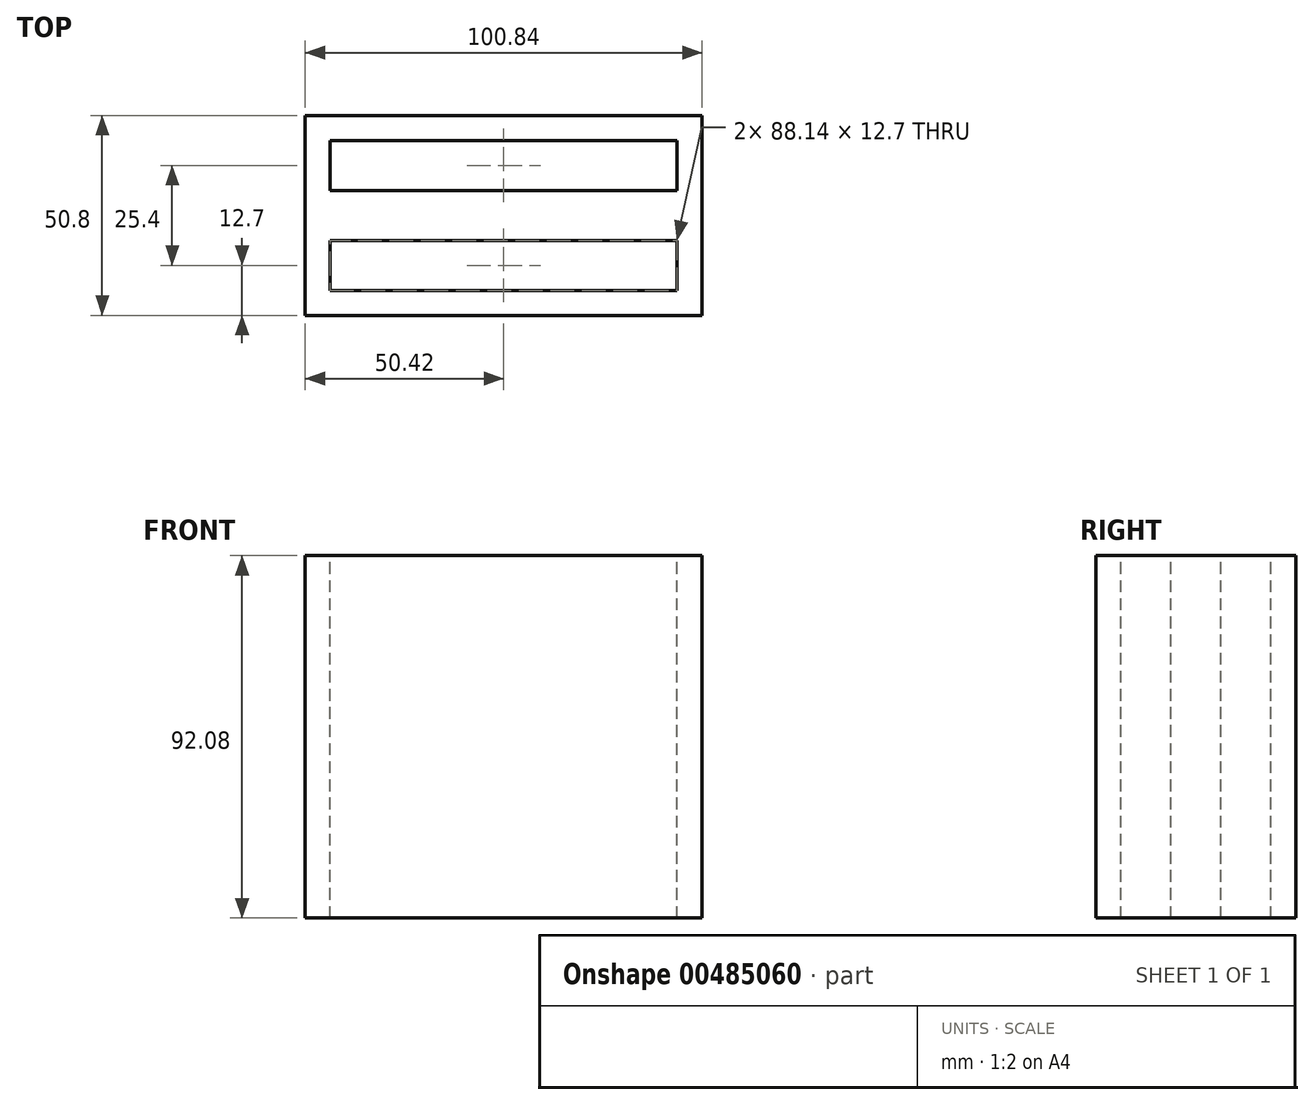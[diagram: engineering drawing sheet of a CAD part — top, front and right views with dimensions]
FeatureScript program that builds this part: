
annotation { "Feature Type Name" : "Feature", "Feature Type Description" : "" }
export const myFeature = defineFeature(function(context is Context, id is Id, definition is map)
    precondition{}
    {
        {
            var Q0;
            Q0=qCreatedBy(makeId("Front.planeOp"),FACE);
            var sketch = newSketch(context, id + "F0", { "sketchPlane" : qUnion([Q0])});
            skLineSegment(sketch, "E0.bottom", {"start": v(50.42, 46.04) * mm, "end": v(-50.42, 46.04) * mm});
            skLineSegment(sketch, "E0.top", {"start": v(50.42, -46.04) * mm, "end": v(-50.42, -46.04) * mm});
            skLineSegment(sketch, "E0.left", {"start": v(50.42, 46.04) * mm, "end": v(50.42, -46.04) * mm});
            skLineSegment(sketch, "E0.right", {"start": v(-50.42, 46.04) * mm, "end": v(-50.42, -46.04) * mm});
            skPoint(sketch, "E0.middle", {"position": v(0, 0) * mm});
            skSolve(sketch);
        }
        {
            var Q0;
            Q0 = qSketchRegion(id + "F0", true);
            extrude(context, id + "F1", {"entities" : qUnion([Q0]), "depth" : 50.8 * mm});
        }
        {
            var Q0;
            Q0=makeQuery(id+"F1.opExtrude","SWEPT_FACE",FACE,{"disambiguationData":[OSD([sQuery(id+"F0.wireOp",EDGE,"E0.bottom")])]});
            var sketch = newSketch(context, id + "F2", { "sketchPlane" : qUnion([Q0])});
            skLineSegment(sketch, "E1", {"start": v(50.42, 0) * mm, "end": v(-50.42, 0) * mm});
            skLineSegment(sketch, "E2.0", {"start": v(-44.07, -31.75) * mm, "end": v(44.07, -31.75) * mm});
            skLineSegment(sketch, "E2.1", {"start": v(-44.07, -31.75) * mm, "end": v(-44.07, -44.45) * mm});
            skLineSegment(sketch, "E2.2", {"start": v(-44.07, -44.45) * mm, "end": v(44.07, -44.45) * mm});
            skLineSegment(sketch, "E2.3", {"start": v(44.07, -44.45) * mm, "end": v(44.07, -31.75) * mm});
            skLineSegment(sketch, "E3.MirrorCS", {"start": v(-44.07, -19.05) * mm, "end": v(44.07, -19.05) * mm});
            skLineSegment(sketch, "E4.MirrorCS", {"start": v(44.07, -6.35) * mm, "end": v(44.07, -19.05) * mm});
            skLineSegment(sketch, "E5.MirrorCS", {"start": v(-44.07, -6.35) * mm, "end": v(44.07, -6.35) * mm});
            skLineSegment(sketch, "E6.MirrorCS", {"start": v(-44.07, -19.05) * mm, "end": v(-44.07, -6.35) * mm});
            skSolve(sketch);
        }
        {
            var Q0;
            Q0=makeQuery(id+"F2.imprint","IMPRINT",FACE,{"disambiguationData":[TD([[makeQuery(id+"F2.imprint","IMPRINT",EDGE,{"derivedFrom":sQuery(id+"F2.wireOp",EDGE,"E3.MirrorCS")}),1.0]])]});
            var Q1;
            Q1=makeQuery(id+"F2.imprint","IMPRINT",FACE,{"disambiguationData":[TD([[makeQuery(id+"F2.imprint","IMPRINT",EDGE,{"derivedFrom":sQuery(id+"F2.wireOp",EDGE,"E2.0")}),-1.0]])]});
            extrude(context, id + "F3", {"entities" : qUnion([Q0, Q1]), "operationType" : NewBodyOperationType.REMOVE, "oppositeDirection" : true, "depth" : 101.6 * mm});
        }
    });
